# Revit family: PRD_FrankeWS_Snks_WorkroomSink_SIRW770_SIRW772
name_source: partatom
category: Plumbing Fixtures
revit_build: Autodesk Revit 2018 (Build: 20190510_1515(x64)
units: mm (PartAtom-declared; Revit-internal decimal feet)

## family parameters
Cut with Voids When Loaded = Yes
Host = Face
OmniClass Number = 23.45.05.14.14.17
OmniClass Title = Plaster Sinks
Part Type = Normal
Room Calculation Point = No
Round Connector Dimension = Use Diameter
Shared = Yes

## types (2) — shared parameters
AssetType = Fixed
BowlDepth = 555.00 mm
BowlFinish = High polished
BowlHeight = 283.00 mm
BowlPosition = Center
Brushes = Without brushes
Category = Pr_40_20_96_81, Sinks
Color = Alpine white
Description = Workroom sink made of MIRANIT resin-bonded mineral material with pore-free smooth surface (temperature-resistant up to 80°C). Basin with integrated tap landing, without tap hole, with marking for drilling holes on the underside of the tap landing. Large inner radii, bottom of basin with 2° slope. Alpine white colour. Stand pipe valve DN 40 x 200 mm and protective strainer (removable) made of stainless steel. Welded substructure frame, powder-coated in basin colour, adjustable base feet. Mounting material included.
DiameterNominal = 40  [stored 0.131234 ft]
DrainSize = 40 mm  [stored 0.131234 ft]
DrainerOrStorage = No
DurationUnit = year
Features = resin-bonded mineral material with pore-free smooth surface
Finish = Coated
Grid = No
IfcExportAs = IfcSanitaryTerminalType
IfcExportType = SINK
IntegralAccessories = incl. mounting material
Manufacturer = KWC Group AG
ManufacturerName = KWC Group AG
ManufacturerURL = www.kwc.com
Material = mineral material
MaterialCode = Miranit
Mounting = Pedestal
NBSDescription = Sinks
NBSReference = 45-35-70/344
NominalDepth = 700 mm  [stored 2.29659 ft]
NominalHeight = 800 mm  [stored 2.62467 ft]
NumberOfWasteHoles = 1
OutletSize = DN 40
Overflow = Standpipe overflow
ProductInformation = https://pim.kwc.com
RearUpstand = No
Shape = Cuboid
SinkMaterial = PRD_AR_ResinBondedMaterial_White
SinkType = Plaster
Spillway = No
Splashback = No
StandMaterial = PRD_AR_Black
StrainerMaterial = PRD_AR_StainlessSteel_SatinFinished
Sump = No
SumpBasket = No
TapLedge = Yes
TypeOfMounting = Wall and floor mounting
TypeOfUtilitySink = Cleaner sink
TypeOfWasteKit = Standpipe strainer
URL = www.kwc.com
Uniclass2015Code = Pr_40_20_96_81
Uniclass2015Title = Sinks
Uniclass2015Version = Products v1.17
UpperEdgeOfBasinHeight = 800.00 mm
Version = 1
WarrantyDurationUnit = year
WashRiffle = No
WasteHolePosition = Center back
WasteHoleProjection = 200.00 mm
WasteKitIncluded = Yes
WasteSize = DN 40
zero-valued in all types: Default Elevation, MountingOffset

## per-type parameters (varying)
| type | BIMObjectName | BowlWidth | GrossWeight | ModelNumber | Name | NetWeight | NominalWidth | Size |
| SIRW770 | PRD_AR_Sinks_WorkroomSink_SIRW770 | 1060.00 mm | 94.00 kg | 2000102720 | Workroom Sink SIRW770 | 89.30 kg | 1100 mm | 1100 x 300/800 x 700 mm (W x H x D) |
| SIRW772 | PRD_AR_Sinks_WorkroomSink_SIRW772 | 1960.00 mm | 165.00 kg | 2000102721 | Workroom Sink SIRW772 | 156.75 kg | 2000 mm  [stored 6.56168 ft] | 2000 x 300/800 x 700 mm (W x H x D) |

note: column(s) folded — value = type name in every type: Model, ModelReference

note: [stored X ft] marks values corroborated as IEEE doubles in the binary element streams (Revit-internal decimal feet)

## geometry (parser evidence)
native form markers: Sweep x6
no freeform markers — native parametric forms only
